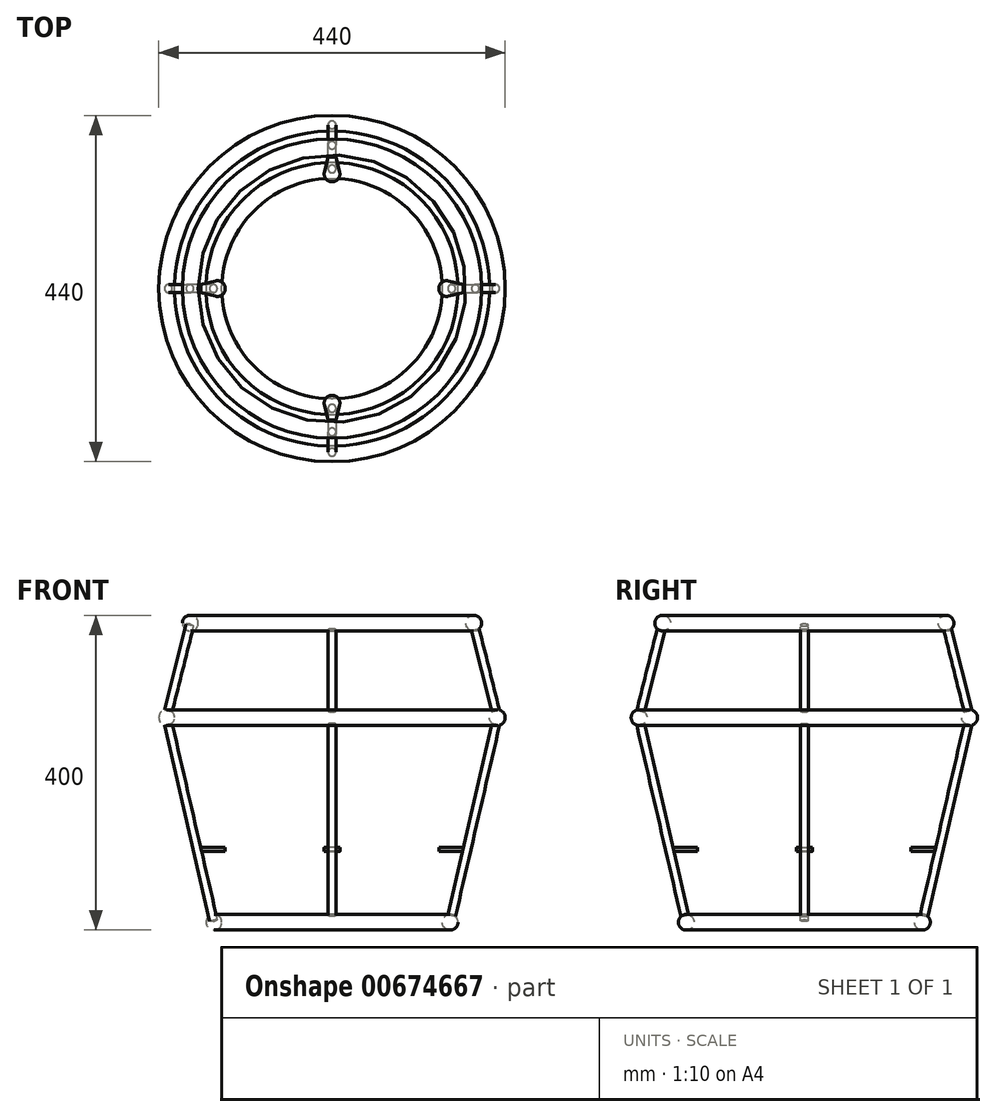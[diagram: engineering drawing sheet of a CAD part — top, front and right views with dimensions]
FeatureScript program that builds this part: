
annotation { "Feature Type Name" : "Feature", "Feature Type Description" : "" }
export const myFeature = defineFeature(function(context is Context, id is Id, definition is map)
    precondition{}
    {
        {
            var Q0;
            Q0=qCreatedBy(makeId("Front.planeOp"),FACE);
            var sketch = newSketch(context, id + "F0", { "sketchPlane" : qUnion([Q0])});
            skCircle(sketch, "E0", {"center": v(210, 0) * mm, "radius": 10 * mm});
            skCircle(sketch, "E1", {"center": v(150, -260) * mm, "radius": 10 * mm});
            skCircle(sketch, "E2", {"center": v(180, 120) * mm, "radius": 10 * mm});
            skLineSegment(sketch, "E3", {"start": v(210, 0) * mm, "end": v(-9.28, 0) * mm, "construction": true});
            skLineSegment(sketch, "E4", {"start": v(0, 0) * mm, "end": v(0, 553.77) * mm, "construction": true});
            skLineSegment(sketch, "E5", {"start": v(180, 120) * mm, "end": v(180.3, 118.79) * mm});
            skLineSegment(sketch, "E6", {"start": v(207.75, -9.74) * mm, "end": v(152.25, -250.26) * mm});
            skLineSegment(sketch, "E7.0", {"start": v(203.18, -7.31) * mm, "end": v(147.08, -250.44) * mm});
            skLineSegment(sketch, "E7.1", {"start": v(177.25, 110.39) * mm, "end": v(203.05, 7.19) * mm});
            skLineSegment(sketch, "E8.0", {"start": v(212.92, -9.56) * mm, "end": v(156.82, -252.69) * mm});
            skLineSegment(sketch, "E8.1", {"start": v(184.85, 121.21) * mm, "end": v(185.46, 118.79) * mm});
            skLineSegment(sketch, "E9.MirrorCS", {"start": v(-175.15, 118.79) * mm, "end": v(-203.05, 7.19) * mm});
            skLineSegment(sketch, "E10.MirrorCS", {"start": v(-184.85, 121.21) * mm, "end": v(-212.75, 9.61) * mm});
            skLineSegment(sketch, "E11.MirrorCS", {"start": v(-203.18, -7.31) * mm, "end": v(-145.13, -258.88) * mm});
            skLineSegment(sketch, "E12.MirrorCS", {"start": v(-212.92, -9.56) * mm, "end": v(-154.87, -261.12) * mm});
            skLineSegment(sketch, "E13.MirrorCS", {"start": v(-180, 120) * mm, "end": v(-207.57, 9.7) * mm});
            skLineSegment(sketch, "E14.MirrorCS", {"start": v(-207.75, -9.74) * mm, "end": v(-150, -260) * mm});
            skLineSegment(sketch, "E15", {"start": v(-145.13, -258.88) * mm, "end": v(-155.4, -258.88) * mm});
            skLineSegment(sketch, "E16", {"start": v(-175.15, 118.79) * mm, "end": v(-185.46, 118.79) * mm});
            skLineSegment(sketch, "E17", {"start": v(175.15, 118.79) * mm, "end": v(185.46, 118.79) * mm});
            skLineSegment(sketch, "E18", {"start": v(145.13, -258.88) * mm, "end": v(155.4, -258.88) * mm});
            skPoint(sketch, "E19.orphan", {"position": v(215.14, 0.05) * mm});
            skLineSegment(sketch, "E20.trimOffspring", {"start": v(204.85, 0) * mm, "end": v(204.86, -0.05) * mm});
            skLineSegment(sketch, "E21.trimOffspring", {"start": v(186.95, 112.81) * mm, "end": v(212.75, 9.61) * mm});
            skLineSegment(sketch, "E22.trimOffspring", {"start": v(182.43, 110.3) * mm, "end": v(207.57, 9.7) * mm});
            skLineSegment(sketch, "E23.trimOffspring", {"start": v(150.26, -258.88) * mm, "end": v(150, -260) * mm});
            skLineSegment(sketch, "E24.trimOffspring", {"start": v(155.4, -258.88) * mm, "end": v(154.87, -261.12) * mm});
            skCircle(sketch, "E25.MirrorC", {"center": v(-210, 0) * mm, "radius": 10 * mm});
            skPoint(sketch, "E26.orphan", {"position": v(-204.86, -0.05) * mm});
            skPoint(sketch, "E27.orphan", {"position": v(-215.14, 0.05) * mm});
            skSolve(sketch);
        }
        {
            var Q0;
            Q0=makeQuery(id+"F0.imprint","IMPRINT",FACE,{"disambiguationData":[TD([[makeQuery(id+"F0.imprint","IMPRINT",EDGE,{"derivedFrom":sQuery(id+"F0.wireOp",EDGE,"E2")}),1.0]])]});
            var Q1;
            Q1=makeQuery(id+"F0.imprint","IMPRINT",FACE,{"disambiguationData":[TD([[makeQuery(id+"F0.imprint","IMPRINT",EDGE,{"derivedFrom":sQuery(id+"F0.wireOp",EDGE,"E0")}),1.0]])]});
            var Q2;
            Q2=makeQuery(id+"F0.imprint","IMPRINT",FACE,{"disambiguationData":[TD([[makeQuery(id+"F0.imprint","IMPRINT",EDGE,{"derivedFrom":sQuery(id+"F0.wireOp",EDGE,"E1")}),1.0]])]});
            var Q3;
            Q3=sQuery(id+"F0.wireOp",EDGE,"E4");
            revolve(context, id + "F1", {"entities" : qUnion([Q0, Q1, Q2]), "axis" : qUnion([Q3]), "revolveType" : RevolveType.FULL});
        }
        {
            var Q0;
            {var subQ0=sQuery(id+"F0.wireOp",EDGE,"E7.1");Q0=makeQuery(id+"F0.imprint","IMPRINT",FACE,{"disambiguationData":[TD([[makeQuery(id+"F0.imprint","IMPRINT",EDGE,{"derivedFrom":subQ0}),1.0]])]});}
            var Q1;
            Q1=sQuery(id+"F0.wireOp",EDGE,"E22.trimOffspring");
            revolve(context, id + "F2", {"entities" : qUnion([Q0]), "axis" : qUnion([Q1]), "revolveType" : RevolveType.FULL});
        }
        {
            var Q0;
            {var subQ0=sQuery(id+"F0.wireOp",EDGE,"E6");Q0=makeQuery(id+"F0.imprint","IMPRINT",FACE,{"disambiguationData":[TD([[makeQuery(id+"F0.imprint","IMPRINT",EDGE,{"derivedFrom":subQ0}),-1.0]])]});}
            var Q1;
            Q1=sQuery(id+"F0.wireOp",EDGE,"E6");
            revolve(context, id + "F3", {"entities" : qUnion([Q0]), "axis" : qUnion([Q1]), "revolveType" : RevolveType.FULL});
        }
        {
            var Q0;
            {var subQ0=sQuery(id+"F0.wireOp",EDGE,"E25.MirrorC");var subQ1=sQuery(id+"F0.wireOp",EDGE,"E10.MirrorCS");var subQ2=makeQuery(id+"F0.imprint","INTERSECT",VERTEX,{"derivedFrom":[subQ1,subQ0]});Q0=makeQuery(id+"F0.imprint","IMPRINT",FACE,{"disambiguationData":[TD([[makeQuery(id+"F0.imprint","IMPRINT",EDGE,{"disambiguationData":[TD([[subQ2,1.0]])],"derivedFrom":subQ1}),1.0]])]});}
            var Q1;
            Q1=sQuery(id+"F0.wireOp",EDGE,"E13.MirrorCS");
            revolve(context, id + "F4", {"entities" : qUnion([Q0]), "axis" : qUnion([Q1]), "revolveType" : RevolveType.FULL});
        }
        {
            var Q0;
            {var subQ0=sQuery(id+"F0.wireOp",EDGE,"E25.MirrorC");var subQ1=sQuery(id+"F0.wireOp",EDGE,"E12.MirrorCS");var subQ2=makeQuery(id+"F0.imprint","INTERSECT",VERTEX,{"derivedFrom":[subQ1,subQ0]});Q0=makeQuery(id+"F0.imprint","IMPRINT",FACE,{"disambiguationData":[TD([[makeQuery(id+"F0.imprint","IMPRINT",EDGE,{"disambiguationData":[TD([[subQ2,-1.0]])],"derivedFrom":subQ1}),1.0]])]});}
            var Q1;
            Q1=sQuery(id+"F0.wireOp",EDGE,"E14.MirrorCS");
            revolve(context, id + "F5", {"entities" : qUnion([Q0]), "axis" : qUnion([Q1]), "revolveType" : RevolveType.FULL});
        }
        {
            var Q0;
            Q0=qCreatedBy(makeId("Right.planeOp"),FACE);
            var sketch = newSketch(context, id + "F6", { "sketchPlane" : qUnion([Q0])});
            skArc(sketch, "E28", {"start": v(-210, -10) * mm, "mid": v(-200, 0) * mm, "end": v(-210, 10) * mm});
            skLineSegment(sketch, "E29", {"start": v(210, -10) * mm, "end": v(-210, -10) * mm});
            skLineSegment(sketch, "E30", {"start": v(210, 10) * mm, "end": v(-210, 10) * mm});
            skArc(sketch, "E31", {"start": v(210, 10) * mm, "mid": v(200, 0) * mm, "end": v(210, -10) * mm});
            skLineSegment(sketch, "E32", {"start": v(180, 110) * mm, "end": v(-180, 110) * mm});
            skLineSegment(sketch, "E33", {"start": v(180, 130) * mm, "end": v(-180, 130) * mm});
            skArc(sketch, "E34", {"start": v(180, 130) * mm, "mid": v(170, 120) * mm, "end": v(180, 110) * mm});
            skArc(sketch, "E35", {"start": v(-180, 110) * mm, "mid": v(-170, 120) * mm, "end": v(-180, 130) * mm});
            skLineSegment(sketch, "E36", {"start": v(150, -270) * mm, "end": v(-150, -270) * mm});
            skLineSegment(sketch, "E37", {"start": v(150, -250) * mm, "end": v(-150, -250) * mm});
            skArc(sketch, "E38", {"start": v(150, -250) * mm, "mid": v(140, -260) * mm, "end": v(150, -270) * mm});
            skArc(sketch, "E39", {"start": v(-150, -270) * mm, "mid": v(-140, -260) * mm, "end": v(-150, -250) * mm});
            skLineSegment(sketch, "E40", {"start": v(-180, 120) * mm, "end": v(-210, 0) * mm});
            skLineSegment(sketch, "E41", {"start": v(-210, 0) * mm, "end": v(-150, -260) * mm});
            skLineSegment(sketch, "E42", {"start": v(180, 120) * mm, "end": v(210, 0) * mm});
            skLineSegment(sketch, "E43", {"start": v(210, 0) * mm, "end": v(150, -260) * mm});
            skLineSegment(sketch, "E44.0", {"start": v(204.86, -0.05) * mm, "end": v(145.13, -258.88) * mm});
            skLineSegment(sketch, "E44.1", {"start": v(175.15, 118.79) * mm, "end": v(204.86, -0.05) * mm});
            skLineSegment(sketch, "E45.0", {"start": v(-215.14, 0.05) * mm, "end": v(-154.87, -261.12) * mm});
            skLineSegment(sketch, "E45.1", {"start": v(-184.85, 121.21) * mm, "end": v(-215.14, 0.05) * mm});
            skCircle(sketch, "E46", {"center": v(-180, 120) * mm, "radius": 10 * mm});
            skCircle(sketch, "E47", {"center": v(-210, 0) * mm, "radius": 10 * mm});
            skCircle(sketch, "E48", {"center": v(-150, -260) * mm, "radius": 10 * mm});
            skCircle(sketch, "E49", {"center": v(150, -260) * mm, "radius": 10 * mm});
            skCircle(sketch, "E50", {"center": v(210, 0) * mm, "radius": 10 * mm});
            skCircle(sketch, "E51", {"center": v(180, 120) * mm, "radius": 10 * mm});
            skLineSegment(sketch, "E52.0", {"start": v(215.14, 0.05) * mm, "end": v(154.87, -261.12) * mm});
            skLineSegment(sketch, "E52.1", {"start": v(184.85, 121.21) * mm, "end": v(215.14, 0.05) * mm});
            skSolve(sketch);
        }
        {
            var Q0;
            {var subQ0=sQuery(id+"F6.wireOp",EDGE,"E46");var subQ3=sQuery(id+"F6.wireOp",EDGE,"E40");var subQ4=makeQuery(id+"F6.imprint","INTERSECT",VERTEX,{"derivedFrom":[subQ3,subQ0]});Q0=makeQuery(id+"F6.imprint","IMPRINT",FACE,{"disambiguationData":[TD([[makeQuery(id+"F6.imprint","IMPRINT",EDGE,{"disambiguationData":[TD([[subQ4,-1.0]])],"derivedFrom":subQ3}),-1.0]])]});}
            var Q1;
            Q1=sQuery(id+"F6.wireOp",EDGE,"E40");
            revolve(context, id + "F7", {"entities" : qUnion([Q0]), "axis" : qUnion([Q1]), "revolveType" : RevolveType.FULL});
        }
        {
            var Q0;
            {var subQ3=sQuery(id+"F6.wireOp",EDGE,"E41");var subQ5=sQuery(id+"F6.wireOp",EDGE,"E48");var subQ6=makeQuery(id+"F6.imprint","INTERSECT",VERTEX,{"derivedFrom":[subQ3,subQ5]});Q0=makeQuery(id+"F6.imprint","IMPRINT",FACE,{"disambiguationData":[TD([[makeQuery(id+"F6.imprint","IMPRINT",EDGE,{"disambiguationData":[TD([[subQ6,1.0]])],"derivedFrom":subQ3}),-1.0]])]});}
            var Q1;
            Q1=sQuery(id+"F6.wireOp",EDGE,"E41");
            revolve(context, id + "F8", {"entities" : qUnion([Q0]), "axis" : qUnion([Q1]), "revolveType" : RevolveType.FULL});
        }
        {
            var Q0;
            {var subQ5=sQuery(id+"F6.wireOp",EDGE,"E51");var subQ7=sQuery(id+"F6.wireOp",EDGE,"E42");var subQ8=makeQuery(id+"F6.imprint","INTERSECT",VERTEX,{"derivedFrom":[subQ7,subQ5]});Q0=makeQuery(id+"F6.imprint","IMPRINT",FACE,{"disambiguationData":[TD([[makeQuery(id+"F6.imprint","IMPRINT",EDGE,{"disambiguationData":[TD([[subQ8,-1.0]])],"derivedFrom":subQ7}),1.0]])]});}
            var Q1;
            Q1=sQuery(id+"F6.wireOp",EDGE,"E42");
            revolve(context, id + "F9", {"entities" : qUnion([Q0]), "axis" : qUnion([Q1]), "revolveType" : RevolveType.FULL});
        }
        {
            var Q0;
            {var subQ5=sQuery(id+"F6.wireOp",EDGE,"E49");var subQ7=sQuery(id+"F6.wireOp",EDGE,"E43");var subQ8=makeQuery(id+"F6.imprint","INTERSECT",VERTEX,{"derivedFrom":[subQ7,subQ5]});Q0=makeQuery(id+"F6.imprint","IMPRINT",FACE,{"disambiguationData":[TD([[makeQuery(id+"F6.imprint","IMPRINT",EDGE,{"disambiguationData":[TD([[subQ8,1.0]])],"derivedFrom":subQ7}),1.0]])]});}
            var Q1;
            Q1=sQuery(id+"F6.wireOp",EDGE,"E43");
            revolve(context, id + "F10", {"entities" : qUnion([Q0]), "axis" : qUnion([Q1]), "revolveType" : RevolveType.FULL});
        }
        {
            var Q0;
            {var subQ1=sQuery(id+"F6.wireOp",EDGE,"E41");var subQ5=sQuery(id+"F6.wireOp",EDGE,"E48");var subQ8=makeQuery(id+"F6.imprint","INTERSECT",VERTEX,{"derivedFrom":[subQ1,subQ5]});Q0=makeQuery(id+"F6.imprint","IMPRINT",FACE,{"disambiguationData":[TD([[makeQuery(id+"F6.imprint","IMPRINT",EDGE,{"disambiguationData":[TD([[subQ8,1.0]])],"derivedFrom":subQ1}),1.0]])]});}
            var sketch = newSketch(context, id + "F11", { "sketchPlane" : qUnion([Q0])});
            skLineSegment(sketch, "E53.0", {"start": v(150, -270) * mm, "end": v(-150, -270) * mm});
            skLineSegment(sketch, "E54", {"start": v(147.08, -250.44) * mm, "end": v(203.18, -7.31) * mm});
            skLineSegment(sketch, "E55", {"start": v(165.64, -170) * mm, "end": v(135.64, -170) * mm});
            skLineSegment(sketch, "E56", {"start": v(135.64, -170) * mm, "end": v(135.64, -165) * mm});
            skLineSegment(sketch, "E57", {"start": v(135.64, -165) * mm, "end": v(166.8, -165) * mm});
            skLineSegment(sketch, "E58", {"start": v(166.8, -165) * mm, "end": v(165.64, -170) * mm});
            skLineSegment(sketch, "E59.MirrorCS", {"start": v(-165.64, -170) * mm, "end": v(-135.64, -170) * mm});
            skLineSegment(sketch, "E60.MirrorCS", {"start": v(-135.64, -165) * mm, "end": v(-166.8, -165) * mm});
            skLineSegment(sketch, "E61.MirrorCS", {"start": v(-135.64, -170) * mm, "end": v(-135.64, -165) * mm});
            skLineSegment(sketch, "E62", {"start": v(-166.8, -165) * mm, "end": v(-165.64, -170) * mm});
            skLineSegment(sketch, "E63", {"start": v(165.64, -170) * mm, "end": v(170.78, -170) * mm});
            skLineSegment(sketch, "E64", {"start": v(170.78, -170) * mm, "end": v(171.94, -165) * mm});
            skLineSegment(sketch, "E65", {"start": v(171.94, -165) * mm, "end": v(166.8, -165) * mm});
            skLineSegment(sketch, "E66", {"start": v(-165.64, -170) * mm, "end": v(-170.81, -170) * mm});
            skLineSegment(sketch, "E67", {"start": v(-170.81, -170) * mm, "end": v(-171.98, -165) * mm});
            skLineSegment(sketch, "E68", {"start": v(-171.98, -165) * mm, "end": v(-166.8, -165) * mm});
            skSolve(sketch);
        }
        {
            var Q0;
            Q0=makeQuery(id+"F11.imprint","IMPRINT",FACE,{"disambiguationData":[TD([[makeQuery(id+"F11.imprint","IMPRINT",EDGE,{"derivedFrom":sQuery(id+"F11.wireOp",EDGE,"E59.MirrorCS")}),1.0]])]});
            var Q1;
            Q1=sQuery(id+"F0.wireOp",EDGE,"E4");
            revolve(context, id + "F12", {"entities" : qUnion([Q0]), "axis" : qUnion([Q1]), "revolveType" : RevolveType.FULL});
        }
        {
            var Q0;
            Q0=makeQuery(id+"F12.opRevolve","SWEPT_FACE",FACE,{"disambiguationData":[OSD([sQuery(id+"F11.wireOp",EDGE,"E60.MirrorCS")])]});
            var sketch = newSketch(context, id + "F13", { "sketchPlane" : qUnion([Q0])});
            skCircle(sketch, "E69", {"center": v(-145.64, 0) * mm, "radius": 10 * mm});
            skCircle(sketch, "E70.MirrorC", {"center": v(145.64, 0) * mm, "radius": 10 * mm});
            skCircle(sketch, "E71", {"center": v(0, 145.64) * mm, "radius": 10 * mm});
            skLineSegment(sketch, "E72", {"start": v(-208.05, 5) * mm, "end": v(-166.72, 5) * mm});
            skLineSegment(sketch, "E73", {"start": v(-166.72, -5) * mm, "end": v(-208.05, -5) * mm});
            skLineSegment(sketch, "E74", {"start": v(-166.72, -5) * mm, "end": v(-148.08, -9.7) * mm});
            skLineSegment(sketch, "E75.MirrorCS", {"start": v(-166.72, 5) * mm, "end": v(-148.08, 9.7) * mm});
            skLineSegment(sketch, "E76.MirrorCS", {"start": v(166.72, 5) * mm, "end": v(148.08, 9.7) * mm});
            skLineSegment(sketch, "E77.MirrorCS", {"start": v(166.72, -5) * mm, "end": v(148.08, -9.7) * mm});
            skLineSegment(sketch, "E78", {"start": v(5, 208.05) * mm, "end": v(5, 166.72) * mm});
            skLineSegment(sketch, "E79", {"start": v(-5, 166.72) * mm, "end": v(-9.7, 148.08) * mm});
            skLineSegment(sketch, "E80.MirrorCS", {"start": v(5, 166.72) * mm, "end": v(9.7, 148.08) * mm});
            skLineSegment(sketch, "E81.trimOffspring", {"start": v(-5, 166.72) * mm, "end": v(-5, 208.05) * mm});
            skLineSegment(sketch, "E82.MirrorCS", {"start": v(5, -166.72) * mm, "end": v(9.7, -148.08) * mm});
            skLineSegment(sketch, "E83.MirrorCS", {"start": v(-5, -166.72) * mm, "end": v(-9.7, -148.08) * mm});
            skCircle(sketch, "E84.MirrorC", {"center": v(0, -145.64) * mm, "radius": 10 * mm});
            skSolve(sketch);
        }
        {
            var Q0;
            {var subQ1=sQuery(id+"F13.wireOp",EDGE,"E76.MirrorCS");Q0=makeQuery(id+"F13.imprint","IMPRINT",FACE,{"disambiguationData":[TD([[makeQuery(id+"F13.imprint","IMPRINT",EDGE,{"derivedFrom":subQ1}),-1.0]])]});}
            var Q1;
            {var subQ5=sQuery(id+"F13.wireOp",EDGE,"E77.MirrorCS");Q1=makeQuery(id+"F13.imprint","IMPRINT",FACE,{"disambiguationData":[TD([[makeQuery(id+"F13.imprint","IMPRINT",EDGE,{"derivedFrom":subQ5}),1.0]])]});}
            var Q2;
            {var subQ7=sQuery(id+"F13.wireOp",EDGE,"E74");Q2=makeQuery(id+"F13.imprint","IMPRINT",FACE,{"disambiguationData":[TD([[makeQuery(id+"F13.imprint","IMPRINT",EDGE,{"derivedFrom":subQ7}),-1.0]])]});}
            var Q3;
            {var subQ5=sQuery(id+"F13.wireOp",EDGE,"E75.MirrorCS");Q3=makeQuery(id+"F13.imprint","IMPRINT",FACE,{"disambiguationData":[TD([[makeQuery(id+"F13.imprint","IMPRINT",EDGE,{"derivedFrom":subQ5}),1.0]])]});}
            extrude(context, id + "F14", {"entities" : qUnion([Q0, Q1, Q2, Q3]), "operationType" : NewBodyOperationType.REMOVE, "oppositeDirection" : true, "depth" : 25 * mm, "offsetDistance" : 25 * mm});
        }
    });
